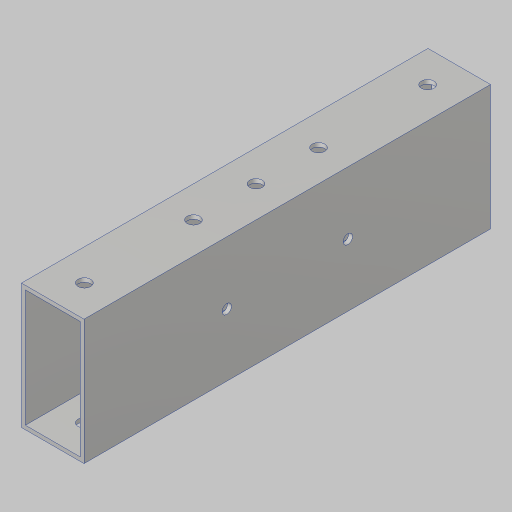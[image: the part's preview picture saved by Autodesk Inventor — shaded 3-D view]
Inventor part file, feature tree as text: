
AUTODESK INVENTOR PART (.ipt)
format: ipt  version: 2023.5 (Build 275446000, 446)  size: 135,680 bytes
history: native  units: in
note: dims shown in document units (in); Inventor stores cm internally (conversion verified against a paired STEP export)
features: hole x3, sketch x3, extrude x1
ambient origin geometry x8: Origin, YZ Plane, XZ Plane, XY Plane, X Axis, Y Axis, Z Axis, Center Point
bodies: Solid1 (feature_tree)
feature tree (7):
  extrude  "Extrusion1"  Depth=1.0in
  hole  "Hole3"  [1 undecoded]
  hole  "Hole4"  [1 undecoded]
  hole  "Hole5"  [1 undecoded]
  sketch  "Sketch5"  dims[d4=0.0in d28=1.0in]
  sketch  "Sketch6"  dims[d29=1.0in]
  sketch  "Sketch7"  dims[d30=0.201in d31=0.75in d32=0.385in d33=0.25in d34=0.5635in d35=1.0in d36=0.8108in d37=5.49in d38=0.201in d39=0.75in d40=0.385in d41=0.25in d42=0.5635in d43=1.0in d44=0.8108in d45=1.9366in d46=0.15in d47=0.75in d48=0.279in d49=0.25in d50=0.5635in d51=1.0in d52=0.8108in]
note: 3 required parameter values undecoded (feature->parameter linkage not recoverable at this tier; creation-order binding heuristic only, values carry confidence <= 0.55)
